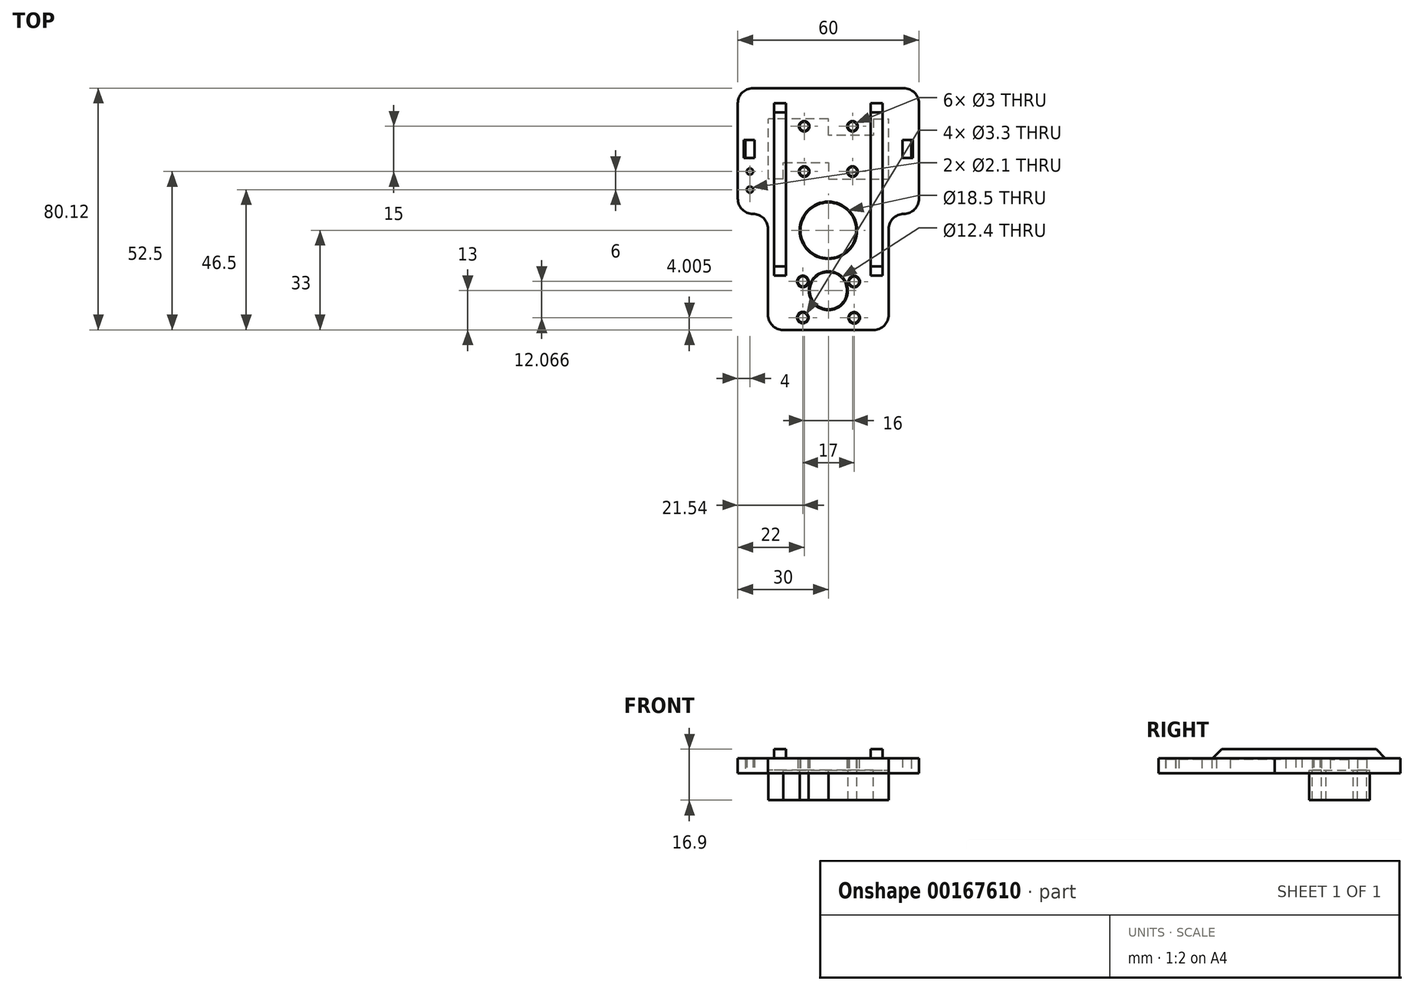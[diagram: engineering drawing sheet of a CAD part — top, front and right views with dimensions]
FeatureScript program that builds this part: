
annotation { "Feature Type Name" : "Feature", "Feature Type Description" : "" }
export const myFeature = defineFeature(function(context is Context, id is Id, definition is map)
    precondition{}
    {
        {
            var Q0;
            Q0=qCreatedBy(makeId("Top.planeOp"),FACE);
            var sketch = newSketch(context, id + "F0", { "sketchPlane" : qUnion([Q0])});
            skLineSegment(sketch, "E0.bottom", {"start": v(0, 0) * mm, "end": v(-19.95, 0) * mm});
            skLineSegment(sketch, "E0.top", {"start": v(0, 10) * mm, "end": v(-19.95, 10) * mm});
            skLineSegment(sketch, "E0.left", {"start": v(0, 0) * mm, "end": v(0, 10) * mm});
            skLineSegment(sketch, "E0.right", {"start": v(-19.95, 0) * mm, "end": v(-19.95, 10) * mm});
            skLineSegment(sketch, "E1", {"start": v(-14.95, 10) * mm, "end": v(-14.95, 0) * mm});
            skLineSegment(sketch, "E2", {"start": v(-14.95, 4.5) * mm, "end": v(0, 4.5) * mm});
            skPoint(sketch, "E2.endSnap0", {"position": v(-14.95, 4.5) * mm});
            skCircle(sketch, "E3", {"center": v(-8, 7.5) * mm, "radius": 1.5 * mm});
            skLineSegment(sketch, "E4", {"start": v(-8, 7.5) * mm, "end": v(0, 7.5) * mm, "construction": true});
            skLineSegment(sketch, "E5", {"start": v(-8, 7.5) * mm, "end": v(-8, 10) * mm, "construction": true});
            skLineSegment(sketch, "E6", {"start": v(0, -15.18) * mm, "end": v(0, -17.23) * mm, "construction": true});
            skLineSegment(sketch, "E7", {"start": v(20.7, 0) * mm, "end": v(22.32, 0) * mm, "construction": true});
            skLineSegment(sketch, "E8.MirrorCS", {"start": v(14.95, 10) * mm, "end": v(14.95, 0) * mm});
            skPoint(sketch, "E9.MirrorP", {"position": v(14.95, 4.5) * mm});
            skLineSegment(sketch, "E10.MirrorCS", {"start": v(19.95, 0) * mm, "end": v(19.95, 10) * mm});
            skLineSegment(sketch, "E11.MirrorCS", {"start": v(0, 10) * mm, "end": v(19.95, 10) * mm});
            skLineSegment(sketch, "E12.MirrorCS", {"start": v(8, 7.5) * mm, "end": v(0, 7.5) * mm, "construction": true});
            skLineSegment(sketch, "E13.MirrorCS", {"start": v(8, 7.5) * mm, "end": v(8, 10) * mm, "construction": true});
            skCircle(sketch, "E14.MirrorC", {"center": v(8, 7.5) * mm, "radius": 1.5 * mm});
            skLineSegment(sketch, "E15.MirrorCS", {"start": v(0, 0) * mm, "end": v(19.95, 0) * mm});
            skLineSegment(sketch, "E16.MirrorCS", {"start": v(14.95, 4.5) * mm, "end": v(0, 4.5) * mm});
            skLineSegment(sketch, "E17.MirrorCS", {"start": v(0, 0) * mm, "end": v(0, -10) * mm});
            skLineSegment(sketch, "E18.MirrorCS", {"start": v(14.95, -4.5) * mm, "end": v(0, -4.5) * mm});
            skLineSegment(sketch, "E19.MirrorCS", {"start": v(-8, -7.5) * mm, "end": v(-8, -10) * mm, "construction": true});
            skLineSegment(sketch, "E20.MirrorCS", {"start": v(0, -10) * mm, "end": v(-19.95, -10) * mm});
            skLineSegment(sketch, "E21.MirrorCS", {"start": v(0, -10) * mm, "end": v(19.95, -10) * mm});
            skCircle(sketch, "E22.MirrorC", {"center": v(-8, -7.5) * mm, "radius": 1.5 * mm});
            skLineSegment(sketch, "E23.MirrorCS", {"start": v(19.95, 0) * mm, "end": v(19.95, -10) * mm});
            skPoint(sketch, "E24.MirrorP", {"position": v(-14.95, -4.5) * mm});
            skLineSegment(sketch, "E25.MirrorCS", {"start": v(-14.95, -4.5) * mm, "end": v(0, -4.5) * mm});
            skLineSegment(sketch, "E26.MirrorCS", {"start": v(-19.95, 0) * mm, "end": v(-19.95, -10) * mm});
            skLineSegment(sketch, "E27.MirrorCS", {"start": v(8, -7.5) * mm, "end": v(0, -7.5) * mm, "construction": true});
            skCircle(sketch, "E28.MirrorC", {"center": v(8, -7.5) * mm, "radius": 1.5 * mm});
            skLineSegment(sketch, "E29.MirrorCS", {"start": v(8, -7.5) * mm, "end": v(8, -10) * mm, "construction": true});
            skLineSegment(sketch, "E30.MirrorCS", {"start": v(-8, -7.5) * mm, "end": v(0, -7.5) * mm, "construction": true});
            skPoint(sketch, "E31.MirrorP", {"position": v(14.95, -4.5) * mm});
            skLineSegment(sketch, "E32.MirrorCS", {"start": v(14.95, -10) * mm, "end": v(14.95, 0) * mm});
            skLineSegment(sketch, "E33.MirrorCS", {"start": v(-14.95, -10) * mm, "end": v(-14.95, 0) * mm});
            skSolve(sketch);
        }
        {
            var Q0;
            {var subQ5=sQuery(id+"F0.wireOp",EDGE,"E18.MirrorCS");Q0=makeQuery(id+"F0.imprint","IMPRINT",FACE,{"disambiguationData":[TD([[makeQuery(id+"F0.imprint","IMPRINT",EDGE,{"derivedFrom":subQ5}),1.0]])]});}
            var Q1;
            {var subQ3=sQuery(id+"F0.wireOp",EDGE,"E25.MirrorCS");Q1=makeQuery(id+"F0.imprint","IMPRINT",FACE,{"disambiguationData":[TD([[makeQuery(id+"F0.imprint","IMPRINT",EDGE,{"derivedFrom":subQ3}),1.0]])]});}
            var Q2;
            {var subQ6=sQuery(id+"F0.wireOp",EDGE,"E0.right");Q2=makeQuery(id+"F0.imprint","IMPRINT",FACE,{"disambiguationData":[TD([[makeQuery(id+"F0.imprint","IMPRINT",EDGE,{"derivedFrom":subQ6}),-1.0]])]});}
            var Q3;
            {var subQ4=sQuery(id+"F0.wireOp",EDGE,"E26.MirrorCS");Q3=makeQuery(id+"F0.imprint","IMPRINT",FACE,{"disambiguationData":[TD([[makeQuery(id+"F0.imprint","IMPRINT",EDGE,{"derivedFrom":subQ4}),1.0]])]});}
            var Q4;
            {var subQ3=sQuery(id+"F0.wireOp",EDGE,"E10.MirrorCS");Q4=makeQuery(id+"F0.imprint","IMPRINT",FACE,{"disambiguationData":[TD([[makeQuery(id+"F0.imprint","IMPRINT",EDGE,{"derivedFrom":subQ3}),1.0]])]});}
            var Q5;
            {var subQ6=sQuery(id+"F0.wireOp",EDGE,"E23.MirrorCS");Q5=makeQuery(id+"F0.imprint","IMPRINT",FACE,{"disambiguationData":[TD([[makeQuery(id+"F0.imprint","IMPRINT",EDGE,{"derivedFrom":subQ6}),-1.0]])]});}
            var Q6;
            Q6=makeQuery(id+"F0.imprint","IMPRINT",FACE,{"disambiguationData":[TD([[makeQuery(id+"F0.imprint","IMPRINT",EDGE,{"derivedFrom":sQuery(id+"F0.wireOp",EDGE,"E22.MirrorC")}),1.0]])]});
            var Q7;
            {var subQ3=sQuery(id+"F0.wireOp",EDGE,"E2");Q7=makeQuery(id+"F0.imprint","IMPRINT",FACE,{"disambiguationData":[TD([[makeQuery(id+"F0.imprint","IMPRINT",EDGE,{"derivedFrom":subQ3}),-1.0]])]});}
            var Q8;
            {var subQ0=sQuery(id+"F0.wireOp",EDGE,"E18.MirrorCS");Q8=makeQuery(id+"F0.imprint","IMPRINT",FACE,{"disambiguationData":[TD([[makeQuery(id+"F0.imprint","IMPRINT",EDGE,{"derivedFrom":subQ0}),-1.0]])]});}
            var Q9;
            {var subQ3=sQuery(id+"F0.wireOp",EDGE,"E16.MirrorCS");Q9=makeQuery(id+"F0.imprint","IMPRINT",FACE,{"disambiguationData":[TD([[makeQuery(id+"F0.imprint","IMPRINT",EDGE,{"derivedFrom":subQ3}),1.0]])]});}
            var Q10;
            Q10=makeQuery(id+"F0.imprint","IMPRINT",FACE,{"disambiguationData":[TD([[makeQuery(id+"F0.imprint","IMPRINT",EDGE,{"derivedFrom":sQuery(id+"F0.wireOp",EDGE,"E14.MirrorC")}),1.0]])]});
            var Q11;
            {var subQ3=sQuery(id+"F0.wireOp",EDGE,"E2");Q11=makeQuery(id+"F0.imprint","IMPRINT",FACE,{"disambiguationData":[TD([[makeQuery(id+"F0.imprint","IMPRINT",EDGE,{"derivedFrom":subQ3}),1.0]])]});}
            extrude(context, id + "F1", {"entities" : qUnion([Q0, Q1, Q2, Q3, Q4, Q5, Q6, Q7, Q8, Q9, Q10, Q11]), "oppositeDirection" : true, "depth" : 9.9 * mm});
        }
        {
            var Q0;
            Q0=makeQuery(id+"F1.opExtrude","CAP_FACE",FACE,{"disambiguationData":[OSD([sQuery(id+"F0.wireOp",EDGE,"E0.top"),sQuery(id+"F0.wireOp",EDGE,"E0.right"),sQuery(id+"F0.wireOp",EDGE,"E3"),sQuery(id+"F0.wireOp",EDGE,"E10.MirrorCS"),sQuery(id+"F0.wireOp",EDGE,"E11.MirrorCS"),sQuery(id+"F0.wireOp",EDGE,"E14.MirrorC"),sQuery(id+"F0.wireOp",EDGE,"E20.MirrorCS"),sQuery(id+"F0.wireOp",EDGE,"E21.MirrorCS"),sQuery(id+"F0.wireOp",EDGE,"E22.MirrorC"),sQuery(id+"F0.wireOp",EDGE,"E23.MirrorCS"),sQuery(id+"F0.wireOp",EDGE,"E26.MirrorCS"),sQuery(id+"F0.wireOp",EDGE,"E28.MirrorC")])],"isStart":true});
            cPlane(context, id + "F2", {"entities" : qUnion([Q0]), "cplaneType" : CPlaneType.OFFSET, "offset" : 1 * mm, "oppositeDirection" : true, "width" : 150 * mm, "height" : 150 * mm});
        }
        {
            var Q0;
            Q0=qCreatedBy(id+"F2.planeOp",FACE);
            var sketch = newSketch(context, id + "F3", { "sketchPlane" : qUnion([Q0])});
            skLineSegment(sketch, "E34", {"start": v(0, 0) * mm, "end": v(0, 25.75) * mm, "construction": true});
            skLineSegment(sketch, "E35", {"start": v(0, 0) * mm, "end": v(0, -37.21) * mm, "construction": true});
            skLineSegment(sketch, "E36", {"start": v(0, 20.12) * mm, "end": v(-25, 20.12) * mm});
            skLineSegment(sketch, "E37", {"start": v(-30, 15.12) * mm, "end": v(-30, -16.52) * mm});
            skLineSegment(sketch, "E38", {"start": v(-25, -21.52) * mm, "end": v(-25, -21.52) * mm});
            skLineSegment(sketch, "E39", {"start": v(-20, -26.52) * mm, "end": v(-20, -55) * mm});
            skLineSegment(sketch, "E40", {"start": v(-15, -60) * mm, "end": v(0, -60) * mm});
            skCircle(sketch, "E41.0", {"center": v(-8, 7.5) * mm, "radius": 1.5 * mm});
            skCircle(sketch, "E42.0", {"center": v(-8, -7.5) * mm, "radius": 1.5 * mm});
            skCircle(sketch, "E43.0", {"center": v(8, 7.5) * mm, "radius": 1.5 * mm});
            skCircle(sketch, "E44.0", {"center": v(8, -7.5) * mm, "radius": 1.5 * mm});
            skLineSegment(sketch, "E45.MirrorCS", {"start": v(0, 20.12) * mm, "end": v(25, 20.12) * mm});
            skLineSegment(sketch, "E46.MirrorCS", {"start": v(30, 15.12) * mm, "end": v(30, -16.52) * mm});
            skLineSegment(sketch, "E47.MirrorCS", {"start": v(25, -21.52) * mm, "end": v(25, -21.52) * mm});
            skLineSegment(sketch, "E48.MirrorCS", {"start": v(20, -26.52) * mm, "end": v(20, -55) * mm});
            skLineSegment(sketch, "E49.MirrorCS", {"start": v(15, -60) * mm, "end": v(0, -60) * mm});
            skCircle(sketch, "E50", {"center": v(0, -47) * mm, "radius": 6.2 * mm});
            skCircle(sketch, "E51", {"center": v(0, -27) * mm, "radius": 9.25 * mm});
            skLineSegment(sketch, "E52", {"start": v(0, 0) * mm, "end": v(-51.1, 0) * mm, "construction": true});
            skLineSegment(sketch, "E53", {"start": v(-27.5, 0) * mm, "end": v(-27.5, 3) * mm});
            skLineSegment(sketch, "E54", {"start": v(-27.5, 3) * mm, "end": v(-24.5, 3) * mm});
            skLineSegment(sketch, "E55", {"start": v(-24.5, 3) * mm, "end": v(-24.5, 0) * mm});
            skLineSegment(sketch, "E56.MirrorCS", {"start": v(-27.5, 0) * mm, "end": v(-27.5, -3) * mm});
            skLineSegment(sketch, "E57.MirrorCS", {"start": v(-27.5, -3) * mm, "end": v(-24.5, -3) * mm});
            skLineSegment(sketch, "E58.MirrorCS", {"start": v(-24.5, -3) * mm, "end": v(-24.5, 0) * mm});
            skLineSegment(sketch, "E59.MirrorCS", {"start": v(24.5, 3) * mm, "end": v(24.5, 0) * mm});
            skLineSegment(sketch, "E60.MirrorCS", {"start": v(27.5, 3) * mm, "end": v(24.5, 3) * mm});
            skLineSegment(sketch, "E61.MirrorCS", {"start": v(27.5, 0) * mm, "end": v(27.5, 3) * mm});
            skLineSegment(sketch, "E62.MirrorCS", {"start": v(27.5, 0) * mm, "end": v(27.5, -3) * mm});
            skLineSegment(sketch, "E63.MirrorCS", {"start": v(27.5, -3) * mm, "end": v(24.5, -3) * mm});
            skLineSegment(sketch, "E64.MirrorCS", {"start": v(24.5, -3) * mm, "end": v(24.5, 0) * mm});
            skPoint(sketch, "E65.visualSharp", {"position": v(-20, -60) * mm});
            skArc(sketch, "E65.filletArc", {"start": v(-20, -55) * mm, "mid": v(-18.54, -58.54) * mm, "end": v(-15, -60) * mm});
            skPoint(sketch, "E66.visualSharp", {"position": v(20, -60) * mm});
            skArc(sketch, "E66.filletArc", {"start": v(15, -60) * mm, "mid": v(18.54, -58.54) * mm, "end": v(20, -55) * mm});
            skPoint(sketch, "E67.visualSharp", {"position": v(20, -21.52) * mm});
            skArc(sketch, "E67.filletArc", {"start": v(25, -21.52) * mm, "mid": v(21.46, -22.99) * mm, "end": v(20, -26.52) * mm});
            skPoint(sketch, "E68.visualSharp", {"position": v(-20, -21.52) * mm});
            skArc(sketch, "E68.filletArc", {"start": v(-20, -26.52) * mm, "mid": v(-21.46, -22.99) * mm, "end": v(-25, -21.52) * mm});
            skPoint(sketch, "E69.visualSharp", {"position": v(-30, 20.12) * mm});
            skArc(sketch, "E69.filletArc", {"start": v(-25, 20.12) * mm, "mid": v(-28.54, 18.66) * mm, "end": v(-30, 15.12) * mm});
            skPoint(sketch, "E70.visualSharp", {"position": v(30, 20.12) * mm});
            skArc(sketch, "E70.filletArc", {"start": v(30, 15.12) * mm, "mid": v(28.54, 18.66) * mm, "end": v(25, 20.12) * mm});
            skPoint(sketch, "E71.visualSharp", {"position": v(30, -21.52) * mm});
            skArc(sketch, "E71.filletArc", {"start": v(25, -21.52) * mm, "mid": v(28.54, -20.06) * mm, "end": v(30, -16.52) * mm});
            skPoint(sketch, "E72.visualSharp", {"position": v(-30, -21.52) * mm});
            skArc(sketch, "E72.filletArc", {"start": v(-30, -16.52) * mm, "mid": v(-28.54, -20.06) * mm, "end": v(-25, -21.52) * mm});
            skCircle(sketch, "E73", {"center": v(-8.46, -43.93) * mm, "radius": 1.65 * mm});
            skCircle(sketch, "E74.MirrorC", {"center": v(8.54, -44) * mm, "radius": 1.65 * mm});
            skCircle(sketch, "E75.MirrorC", {"center": v(-8.46, -55.93) * mm, "radius": 1.65 * mm});
            skCircle(sketch, "E76.MirrorC", {"center": v(8.54, -56) * mm, "radius": 1.65 * mm});
            skCircle(sketch, "E77", {"center": v(-26, -7.5) * mm, "radius": 1.05 * mm});
            skCircle(sketch, "E78", {"center": v(-26, -13.5) * mm, "radius": 1.05 * mm});
            skLineSegment(sketch, "E79", {"start": v(-26, -7.5) * mm, "end": v(-26, -13.5) * mm, "construction": true});
            skLineSegment(sketch, "E80", {"start": v(-8.46, -43.93) * mm, "end": v(8.54, -44) * mm, "construction": true});
            skLineSegment(sketch, "E81", {"start": v(-8.46, -55.93) * mm, "end": v(8.54, -44) * mm, "construction": true});
            skLineSegment(sketch, "E82", {"start": v(-8.46, -55.93) * mm, "end": v(8.54, -56) * mm, "construction": true});
            skLineSegment(sketch, "E83", {"start": v(8.54, -44) * mm, "end": v(8.54, -56) * mm, "construction": true});
            skLineSegment(sketch, "E84", {"start": v(-8.46, -43.93) * mm, "end": v(-8.46, -55.93) * mm, "construction": true});
            skSolve(sketch);
        }
        {
            var Q0;
            Q0=makeQuery(id+"F3.imprint","IMPRINT",FACE,{"disambiguationData":[TD([[makeQuery(id+"F3.imprint","IMPRINT",EDGE,{"derivedFrom":sQuery(id+"F3.wireOp",EDGE,"E36")}),1.0]])]});
            extrude(context, id + "F4", {"entities" : qUnion([Q0]), "depth" : 5 * mm});
        }
        {
            var Q0;
            Q0=makeQuery(id+"F4.opExtrude","CAP_EDGE",EDGE,{"disambiguationData":[OSD([sQuery(id+"F3.wireOp",EDGE,"E44.0")])],"isStart":false});
            var Q1;
            Q1=makeQuery(id+"F4.opExtrude","CAP_EDGE",EDGE,{"disambiguationData":[OSD([sQuery(id+"F3.wireOp",EDGE,"E43.0")])],"isStart":false});
            var Q2;
            Q2=makeQuery(id+"F4.opExtrude","CAP_EDGE",EDGE,{"disambiguationData":[OSD([sQuery(id+"F3.wireOp",EDGE,"E41.0")])],"isStart":false});
            var Q3;
            Q3=makeQuery(id+"F4.opExtrude","CAP_EDGE",EDGE,{"disambiguationData":[OSD([sQuery(id+"F3.wireOp",EDGE,"E42.0")])],"isStart":false});
            var Q4;
            Q4=makeQuery(id+"F4.opExtrude","CAP_EDGE",EDGE,{"disambiguationData":[OSD([sQuery(id+"F3.wireOp",EDGE,"E73")])],"isStart":false});
            var Q5;
            Q5=makeQuery(id+"F4.opExtrude","CAP_EDGE",EDGE,{"disambiguationData":[OSD([sQuery(id+"F3.wireOp",EDGE,"E74.MirrorC")])],"isStart":false});
            var Q6;
            Q6=makeQuery(id+"F4.opExtrude","CAP_EDGE",EDGE,{"disambiguationData":[OSD([sQuery(id+"F3.wireOp",EDGE,"E76.MirrorC")])],"isStart":false});
            var Q7;
            Q7=makeQuery(id+"F4.opExtrude","CAP_EDGE",EDGE,{"disambiguationData":[OSD([sQuery(id+"F3.wireOp",EDGE,"E75.MirrorC")])],"isStart":false});
            var Q8;
            Q8=makeQuery(id+"F4.opExtrude","CAP_EDGE",EDGE,{"disambiguationData":[OSD([sQuery(id+"F3.wireOp",EDGE,"E50")])],"isStart":false});
            var Q9;
            Q9=makeQuery(id+"F4.opExtrude","CAP_EDGE",EDGE,{"disambiguationData":[OSD([sQuery(id+"F3.wireOp",EDGE,"E51")])],"isStart":false});
            chamfer(context, id + "F5", {"entities" : qUnion([Q0, Q1, Q2, Q3, Q4, Q5, Q6, Q7, Q8, Q9]), "chamferType" : ChamferType.OFFSET_ANGLE, "width" : 0.25 * mm, "oppositeDirection" : false, "angle" : 45 * degree, "tangentPropagation" : true});
        }
        {
            var Q0;
            Q0=makeQuery(id+"F4.opExtrude","CAP_EDGE",EDGE,{"disambiguationData":[OSD([sQuery(id+"F3.wireOp",EDGE,"E53"),sQuery(id+"F3.wireOp",EDGE,"E56.MirrorCS")])],"isStart":false});
            var Q1;
            Q1=makeQuery(id+"F4.opExtrude","CAP_EDGE",EDGE,{"disambiguationData":[OSD([sQuery(id+"F3.wireOp",EDGE,"E61.MirrorCS"),sQuery(id+"F3.wireOp",EDGE,"E62.MirrorCS")])],"isStart":false});
            chamfer(context, id + "F6", {"entities" : qUnion([Q0, Q1]), "width" : 0.5 * mm, "tangentPropagation" : true});
        }
        {
            var Q0;
            Q0=makeQuery(id+"F4.opExtrude","CAP_FACE",FACE,{"disambiguationData":[OSD([sQuery(id+"F3.wireOp",EDGE,"E36"),sQuery(id+"F3.wireOp",EDGE,"E37"),sQuery(id+"F3.wireOp",EDGE,"E39"),sQuery(id+"F3.wireOp",EDGE,"E40"),sQuery(id+"F3.wireOp",EDGE,"E41.0"),sQuery(id+"F3.wireOp",EDGE,"E42.0"),sQuery(id+"F3.wireOp",EDGE,"E43.0"),sQuery(id+"F3.wireOp",EDGE,"E44.0"),sQuery(id+"F3.wireOp",EDGE,"E45.MirrorCS"),sQuery(id+"F3.wireOp",EDGE,"E46.MirrorCS"),sQuery(id+"F3.wireOp",EDGE,"E48.MirrorCS"),sQuery(id+"F3.wireOp",EDGE,"E49.MirrorCS"),sQuery(id+"F3.wireOp",EDGE,"E50"),sQuery(id+"F3.wireOp",EDGE,"E51"),sQuery(id+"F3.wireOp",EDGE,"E53"),sQuery(id+"F3.wireOp",EDGE,"E54"),sQuery(id+"F3.wireOp",EDGE,"E55"),sQuery(id+"F3.wireOp",EDGE,"E56.MirrorCS"),sQuery(id+"F3.wireOp",EDGE,"E57.MirrorCS"),sQuery(id+"F3.wireOp",EDGE,"E58.MirrorCS"),sQuery(id+"F3.wireOp",EDGE,"E59.MirrorCS"),sQuery(id+"F3.wireOp",EDGE,"E60.MirrorCS"),sQuery(id+"F3.wireOp",EDGE,"E61.MirrorCS"),sQuery(id+"F3.wireOp",EDGE,"E62.MirrorCS"),sQuery(id+"F3.wireOp",EDGE,"E63.MirrorCS"),sQuery(id+"F3.wireOp",EDGE,"E64.MirrorCS"),sQuery(id+"F3.wireOp",EDGE,"E65.filletArc"),sQuery(id+"F3.wireOp",EDGE,"E66.filletArc"),sQuery(id+"F3.wireOp",EDGE,"E67.filletArc"),sQuery(id+"F3.wireOp",EDGE,"E68.filletArc"),sQuery(id+"F3.wireOp",EDGE,"E69.filletArc"),sQuery(id+"F3.wireOp",EDGE,"E70.filletArc"),sQuery(id+"F3.wireOp",EDGE,"E71.filletArc"),sQuery(id+"F3.wireOp",EDGE,"E72.filletArc"),sQuery(id+"F3.wireOp",EDGE,"E73"),sQuery(id+"F3.wireOp",EDGE,"E74.MirrorC"),sQuery(id+"F3.wireOp",EDGE,"E75.MirrorC"),sQuery(id+"F3.wireOp",EDGE,"E76.MirrorC"),sQuery(id+"F3.wireOp",EDGE,"E77"),sQuery(id+"F3.wireOp",EDGE,"E78")])],"isStart":false});
            var sketch = newSketch(context, id + "F7", { "sketchPlane" : qUnion([Q0])});
            skLineSegment(sketch, "E85.bottom", {"start": v(-18, 17.12) * mm, "end": v(-14, 17.12) * mm});
            skLineSegment(sketch, "E85.top", {"start": v(-18, -44) * mm, "end": v(-14, -44) * mm});
            skLineSegment(sketch, "E85.left", {"start": v(-18, 17.12) * mm, "end": v(-18, -44) * mm});
            skLineSegment(sketch, "E85.right", {"start": v(-14, 17.12) * mm, "end": v(-14, -44) * mm});
            skLineSegment(sketch, "E86.MirrorCS", {"start": v(14, 17.12) * mm, "end": v(14, -44) * mm});
            skLineSegment(sketch, "E87.MirrorCS", {"start": v(18, 17.12) * mm, "end": v(14, 17.12) * mm});
            skLineSegment(sketch, "E88.MirrorCS", {"start": v(18, 17.12) * mm, "end": v(18, -44) * mm});
            skLineSegment(sketch, "E89.MirrorCS", {"start": v(18, -44) * mm, "end": v(14, -44) * mm});
            skSolve(sketch);
        }
        {
            var Q0;
            Q0=makeQuery(id+"F7.imprint","IMPRINT",FACE,{"disambiguationData":[TD([[makeQuery(id+"F7.imprint","IMPRINT",EDGE,{"derivedFrom":sQuery(id+"F7.wireOp",EDGE,"E85.bottom")}),-1.0]])]});
            var Q1;
            Q1=makeQuery(id+"F7.imprint","IMPRINT",FACE,{"disambiguationData":[TD([[makeQuery(id+"F7.imprint","IMPRINT",EDGE,{"derivedFrom":sQuery(id+"F7.wireOp",EDGE,"E86.MirrorCS")}),1.0]])]});
            extrude(context, id + "F8", {"entities" : qUnion([Q0, Q1]), "operationType" : NewBodyOperationType.ADD, "depth" : 3 * mm});
        }
        {
            var Q0;
            Q0=makeQuery(id+"F8.opExtrude","CAP_EDGE",EDGE,{"disambiguationData":[OSD([sQuery(id+"F7.wireOp",EDGE,"E85.top")])],"isStart":false});
            var Q1;
            Q1=makeQuery(id+"F8.opExtrude","CAP_EDGE",EDGE,{"disambiguationData":[OSD([sQuery(id+"F7.wireOp",EDGE,"E89.MirrorCS")])],"isStart":false});
            var Q2;
            Q2=makeQuery(id+"F8.opExtrude","CAP_EDGE",EDGE,{"disambiguationData":[OSD([sQuery(id+"F7.wireOp",EDGE,"E85.bottom")])],"isStart":false});
            var Q3;
            Q3=makeQuery(id+"F8.opExtrude","CAP_EDGE",EDGE,{"disambiguationData":[OSD([sQuery(id+"F7.wireOp",EDGE,"E87.MirrorCS")])],"isStart":false});
            chamfer(context, id + "F9", {"entities" : qUnion([Q0, Q1, Q2, Q3]), "width" : 5 * mm, "tangentPropagation" : true});
        }
    });
